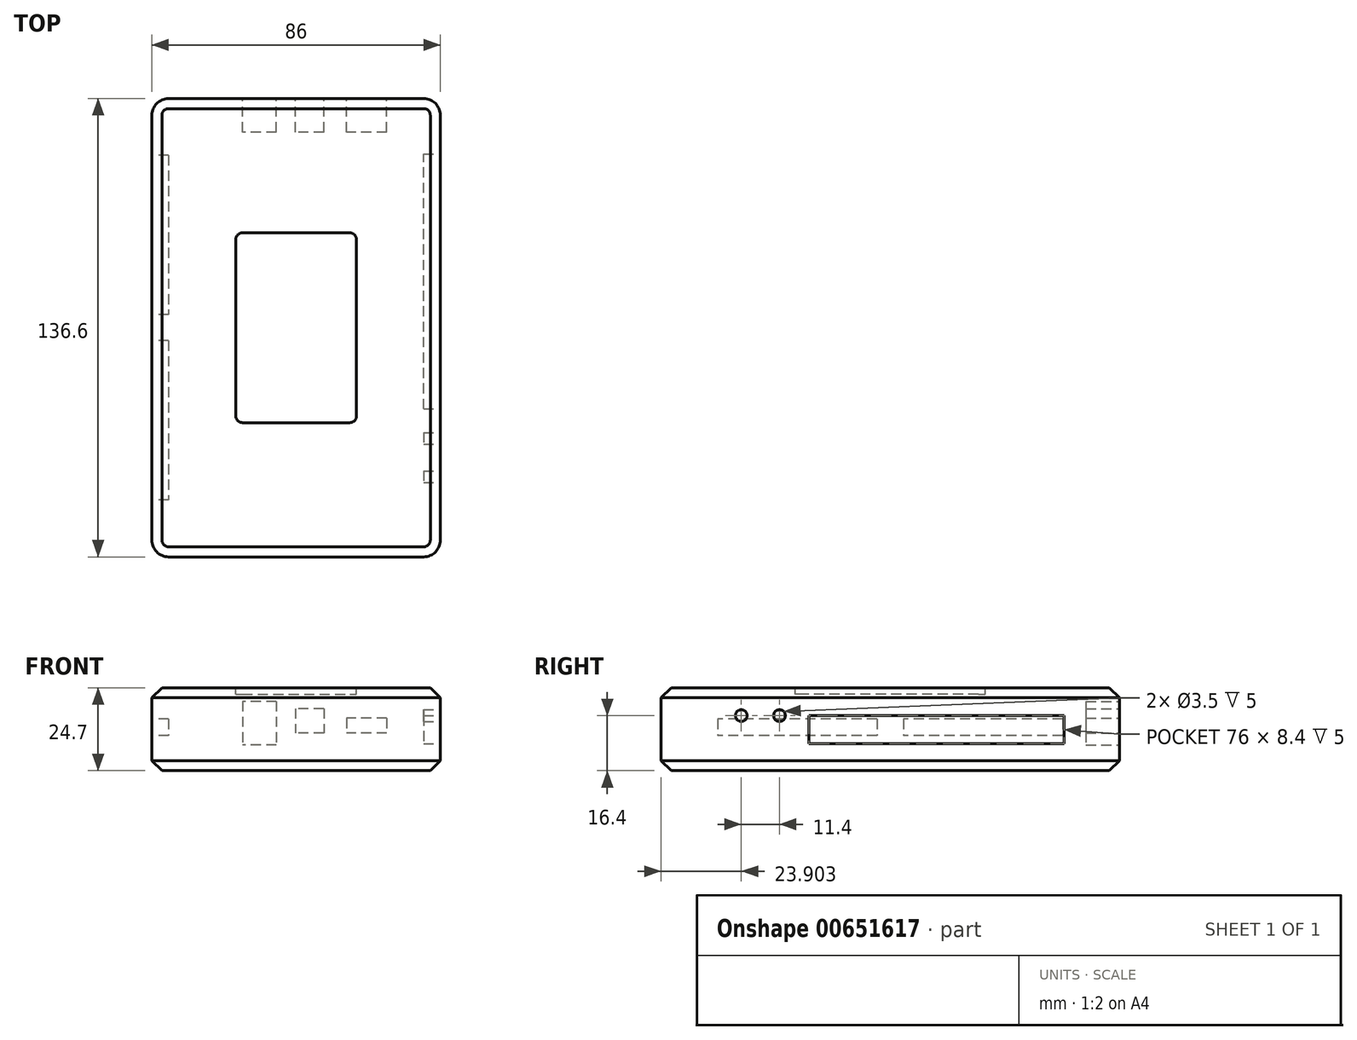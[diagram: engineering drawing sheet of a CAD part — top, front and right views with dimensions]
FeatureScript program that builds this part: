
annotation { "Feature Type Name" : "Feature", "Feature Type Description" : "" }
export const myFeature = defineFeature(function(context is Context, id is Id, definition is map)
    precondition{}
    {
        {
            var Q0;
            Q0=qCreatedBy(makeId("Top.planeOp"),FACE);
            var sketch = newSketch(context, id + "F0", { "sketchPlane" : qUnion([Q0])});
            skLineSegment(sketch, "E0.bottom", {"start": v(-51.87, 69.77) * mm, "end": v(34.13, 69.77) * mm});
            skLineSegment(sketch, "E0.top", {"start": v(-51.87, -66.83) * mm, "end": v(34.13, -66.83) * mm});
            skLineSegment(sketch, "E0.left", {"start": v(-51.87, 69.77) * mm, "end": v(-51.87, -66.83) * mm});
            skLineSegment(sketch, "E0.right", {"start": v(34.13, 69.77) * mm, "end": v(34.13, -66.83) * mm});
            skSolve(sketch);
        }
        {
            var Q0;
            Q0=makeQuery(id+"F0.imprint","IMPRINT",FACE,{"disambiguationData":[TD([[makeQuery(id+"F0.imprint","IMPRINT",EDGE,{"derivedFrom":sQuery(id+"F0.wireOp",EDGE,"E0.bottom")}),-1.0]])]});
            extrude(context, id + "F1", {"entities" : qUnion([Q0]), "depth" : 24.7 * mm, "offsetDistance" : 25 * mm});
        }
        {
            var Q0;
            Q0=makeQuery(id+"F1.opExtrude","SWEPT_FACE",FACE,{"disambiguationData":[OSD([sQuery(id+"F0.wireOp",EDGE,"E0.bottom")])]});
            var sketch = newSketch(context, id + "F2", { "sketchPlane" : qUnion([Q0])});
            skLineSegment(sketch, "E1.bottom", {"start": v(-18.13, 15.65) * mm, "end": v(-6.13, 15.65) * mm});
            skLineSegment(sketch, "E1.top", {"start": v(-18.13, 11.15) * mm, "end": v(-6.13, 11.15) * mm});
            skLineSegment(sketch, "E1.left", {"start": v(-18.13, 15.65) * mm, "end": v(-18.13, 11.15) * mm});
            skLineSegment(sketch, "E1.right", {"start": v(-6.13, 15.65) * mm, "end": v(-6.13, 11.15) * mm});
            skLineSegment(sketch, "E2.bottom", {"start": v(0.62, 18.45) * mm, "end": v(9.12, 18.45) * mm});
            skLineSegment(sketch, "E2.top", {"start": v(0.62, 11.15) * mm, "end": v(9.12, 11.15) * mm});
            skLineSegment(sketch, "E2.left", {"start": v(0.62, 18.45) * mm, "end": v(0.62, 11.15) * mm});
            skLineSegment(sketch, "E2.right", {"start": v(9.12, 18.45) * mm, "end": v(9.12, 11.15) * mm});
            skLineSegment(sketch, "E3.bottom", {"start": v(14.77, 20.65) * mm, "end": v(24.77, 20.65) * mm});
            skLineSegment(sketch, "E3.top", {"start": v(14.77, 7.65) * mm, "end": v(24.77, 7.65) * mm});
            skLineSegment(sketch, "E3.left", {"start": v(14.77, 20.65) * mm, "end": v(14.77, 7.65) * mm});
            skLineSegment(sketch, "E3.right", {"start": v(24.77, 20.65) * mm, "end": v(24.77, 7.65) * mm});
            skSolve(sketch);
        }
        {
            var Q0;
            Q0=makeQuery(id+"F1.opExtrude","SWEPT_EDGE",EDGE,{"disambiguationData":[OSD([sQuery(id+"F0.wireOp",EDGE,"E0.top"),sQuery(id+"F0.wireOp",EDGE,"E0.left")])]});
            var Q1;
            Q1=makeQuery(id+"F1.opExtrude","SWEPT_EDGE",EDGE,{"disambiguationData":[OSD([sQuery(id+"F0.wireOp",EDGE,"E0.top"),sQuery(id+"F0.wireOp",EDGE,"E0.right")])]});
            var Q2;
            Q2=makeQuery(id+"F1.opExtrude","SWEPT_EDGE",EDGE,{"disambiguationData":[OSD([sQuery(id+"F0.wireOp",EDGE,"E0.bottom"),sQuery(id+"F0.wireOp",EDGE,"E0.right")])]});
            var Q3;
            Q3=makeQuery(id+"F1.opExtrude","SWEPT_EDGE",EDGE,{"disambiguationData":[OSD([sQuery(id+"F0.wireOp",EDGE,"E0.bottom"),sQuery(id+"F0.wireOp",EDGE,"E0.left")])]});
            fillet(context, id + "F3", {"entities" : qUnion([Q0, Q1, Q2, Q3]), "radius" : 5 * mm, "tangentPropagation" : true, "allowEdgeOverflow" : false});
        }
        {
            var Q0;
            Q0=makeQuery(id+"F1.opExtrude","CAP_FACE",FACE,{"disambiguationData":[OSD([sQuery(id+"F0.wireOp",EDGE,"E0.bottom"),sQuery(id+"F0.wireOp",EDGE,"E0.top"),sQuery(id+"F0.wireOp",EDGE,"E0.left"),sQuery(id+"F0.wireOp",EDGE,"E0.right")])],"isStart":false});
            var Q1;
            Q1=makeQuery(id+"F1.opExtrude","CAP_FACE",FACE,{"disambiguationData":[OSD([sQuery(id+"F0.wireOp",EDGE,"E0.bottom"),sQuery(id+"F0.wireOp",EDGE,"E0.top"),sQuery(id+"F0.wireOp",EDGE,"E0.left"),sQuery(id+"F0.wireOp",EDGE,"E0.right")])],"isStart":true});
            chamfer(context, id + "F4", {"entities" : qUnion([Q0, Q1]), "width" : 3 * mm, "tangentPropagation" : true});
        }
        {
            var Q0;
            Q0=makeQuery(id+"F1.opExtrude","CAP_FACE",FACE,{"disambiguationData":[OSD([sQuery(id+"F0.wireOp",EDGE,"E0.bottom"),sQuery(id+"F0.wireOp",EDGE,"E0.top"),sQuery(id+"F0.wireOp",EDGE,"E0.left"),sQuery(id+"F0.wireOp",EDGE,"E0.right")])],"isStart":false});
            var sketch = newSketch(context, id + "F5", { "sketchPlane" : qUnion([Q0])});
            skLineSegment(sketch, "E4.bottom", {"start": v(-24.87, 29.77) * mm, "end": v(7.13, 29.77) * mm});
            skLineSegment(sketch, "E4.top", {"start": v(-24.87, -26.83) * mm, "end": v(7.13, -26.83) * mm});
            skLineSegment(sketch, "E4.left", {"start": v(-26.87, 27.77) * mm, "end": v(-26.87, -24.83) * mm});
            skLineSegment(sketch, "E4.right", {"start": v(9.13, 27.77) * mm, "end": v(9.13, -24.83) * mm});
            skPoint(sketch, "E5.visualSharp", {"position": v(-26.87, 29.77) * mm});
            skArc(sketch, "E5.filletArc", {"start": v(-24.87, 29.77) * mm, "mid": v(-26.29, 29.19) * mm, "end": v(-26.87, 27.77) * mm});
            skPoint(sketch, "E6.visualSharp", {"position": v(9.13, -26.83) * mm});
            skArc(sketch, "E6.filletArc", {"start": v(7.13, -26.83) * mm, "mid": v(8.54, -26.24) * mm, "end": v(9.13, -24.83) * mm});
            skPoint(sketch, "E7.visualSharp", {"position": v(-26.87, -26.83) * mm});
            skArc(sketch, "E7.filletArc", {"start": v(-26.87, -24.83) * mm, "mid": v(-26.29, -26.24) * mm, "end": v(-24.87, -26.83) * mm});
            skPoint(sketch, "E8.visualSharp", {"position": v(9.13, 29.77) * mm});
            skArc(sketch, "E8.filletArc", {"start": v(9.13, 27.77) * mm, "mid": v(8.54, 29.19) * mm, "end": v(7.13, 29.77) * mm});
            skSolve(sketch);
        }
        {
            var Q0;
            Q0 = qSketchRegion(id + "F5", true);
            extrude(context, id + "F6", {"entities" : qUnion([Q0]), "operationType" : NewBodyOperationType.REMOVE, "oppositeDirection" : true, "depth" : 2 * mm, "offsetDistance" : 25 * mm});
        }
        {
            var Q0;
            Q0=makeQuery(id+"F1.opExtrude","SWEPT_FACE",FACE,{"disambiguationData":[OSD([sQuery(id+"F0.wireOp",EDGE,"E0.left")])]});
            var sketch = newSketch(context, id + "F7", { "sketchPlane" : qUnion([Q0])});
            skLineSegment(sketch, "E9.bottom", {"start": v(-52.87, 15.4) * mm, "end": v(-5.37, 15.4) * mm});
            skLineSegment(sketch, "E9.top", {"start": v(-52.87, 10.4) * mm, "end": v(-5.37, 10.4) * mm});
            skLineSegment(sketch, "E9.left", {"start": v(-52.87, 15.4) * mm, "end": v(-52.87, 10.4) * mm});
            skLineSegment(sketch, "E9.right", {"start": v(-5.37, 15.4) * mm, "end": v(-5.37, 10.4) * mm});
            skLineSegment(sketch, "E10.bottom", {"start": v(2.43, 15.4) * mm, "end": v(49.93, 15.4) * mm});
            skLineSegment(sketch, "E10.top", {"start": v(2.43, 10.4) * mm, "end": v(49.93, 10.4) * mm});
            skLineSegment(sketch, "E10.left", {"start": v(2.43, 15.4) * mm, "end": v(2.43, 10.4) * mm});
            skLineSegment(sketch, "E10.right", {"start": v(49.93, 15.4) * mm, "end": v(49.93, 10.4) * mm});
            skSolve(sketch);
        }
        {
            var Q0;
            Q0 = qSketchRegion(id + "F7", true);
            extrude(context, id + "F8", {"entities" : qUnion([Q0]), "operationType" : NewBodyOperationType.REMOVE, "oppositeDirection" : true, "depth" : 5 * mm, "offsetDistance" : 25 * mm});
        }
        {
            var Q0;
            Q0 = qSketchRegion(id + "F2", true);
            extrude(context, id + "F9", {"entities" : qUnion([Q0]), "operationType" : NewBodyOperationType.REMOVE, "oppositeDirection" : true, "depth" : 10 * mm, "offsetDistance" : 25 * mm});
        }
        {
            var Q0;
            Q0=makeQuery(id+"F1.opExtrude","SWEPT_FACE",FACE,{"disambiguationData":[OSD([sQuery(id+"F0.wireOp",EDGE,"E0.right")])]});
            var sketch = newSketch(context, id + "F10", { "sketchPlane" : qUnion([Q0])});
            skLineSegment(sketch, "E11.bottom", {"start": v(-22.73, 16.4) * mm, "end": v(53.27, 16.4) * mm});
            skLineSegment(sketch, "E11.top", {"start": v(-22.73, 8) * mm, "end": v(53.27, 8) * mm});
            skLineSegment(sketch, "E11.left", {"start": v(-22.73, 16.4) * mm, "end": v(-22.73, 8) * mm});
            skLineSegment(sketch, "E11.right", {"start": v(53.27, 16.4) * mm, "end": v(53.27, 8) * mm});
            skCircle(sketch, "E12", {"center": v(-42.93, 16.4) * mm, "radius": 1.75 * mm});
            skCircle(sketch, "E13", {"center": v(-31.53, 16.4) * mm, "radius": 1.75 * mm});
            skSolve(sketch);
        }
        {
            var Q0;
            Q0 = qSketchRegion(id + "F10", true);
            extrude(context, id + "F11", {"entities" : qUnion([Q0]), "operationType" : NewBodyOperationType.REMOVE, "oppositeDirection" : true, "depth" : 5 * mm, "offsetDistance" : 25 * mm});
        }
    });
